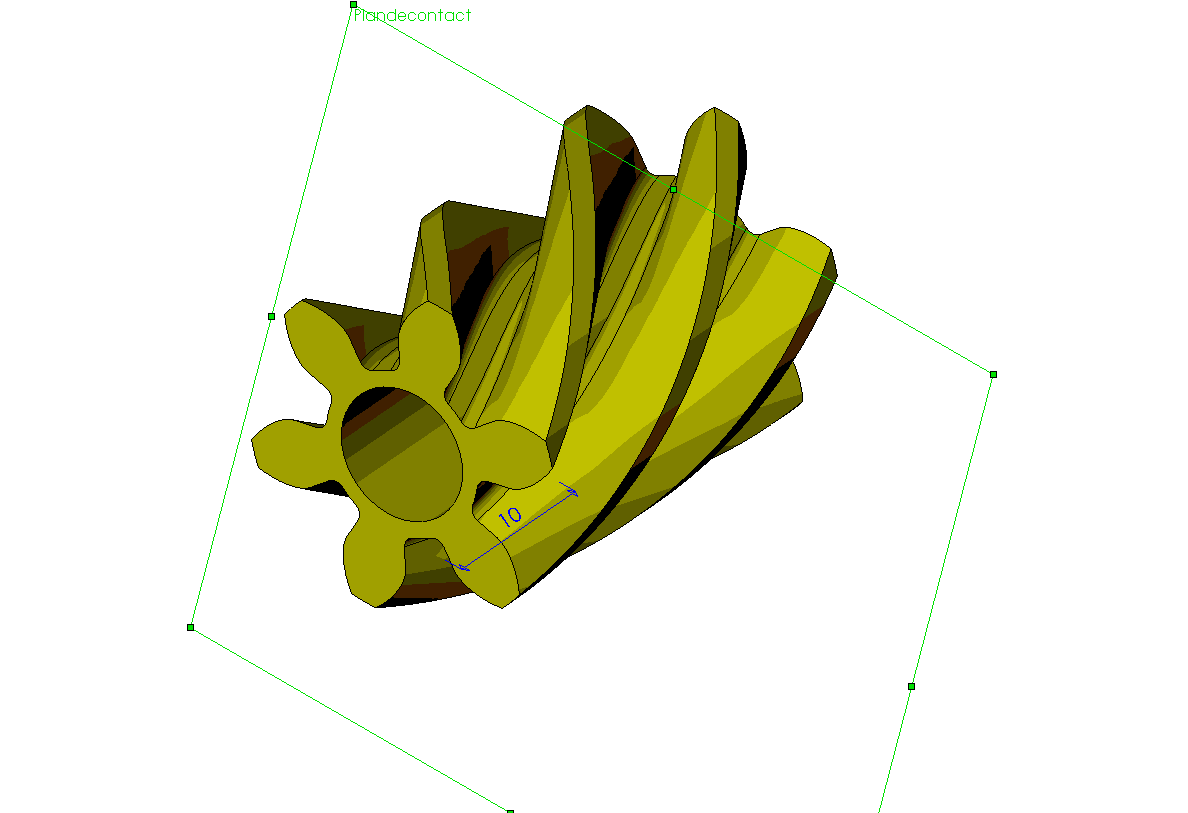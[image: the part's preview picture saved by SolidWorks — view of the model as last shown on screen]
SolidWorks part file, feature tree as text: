
SOLIDWORKS PART (.sldprt)
format: sldprt  version: not decoded by parser v0  size: 2,865,152 bytes
history: native  units: mm
features: sketch x9, plane x6, material x1, extrude x1, helix x1, sweep x1, pattern_circular x1, cut_extrude x1 (+8 scaffold rows collapsed)
feature tree (29):
  scaffold x8  (default folders/planes/origin — collapsed)
  material  "Matériau <non spécifié>"
  plane  "Plan1"
  plane  "Plan2"
  plane  "Plan3"
  plane  "Plandecontact"  Offset=10mm
  sketch  "def"  dims[c1.D1=10.0mm c1.D2=1.0mm c1.D3=1.0mm c1.D4=0.3mm c1.D5=~14.911604mm c2.D1=6.0mm c2.D6=~8.457328mm c2.D2=2.0mm c2.D7=~6.009154mm c2.D3=1.0mm c2.D8=~2.819109mm c2.D4=0.3mm c2.D5=25.0mm c3.D6=1.0mm c3.D7=30.0mm c3.D8=~13.540468mm c3.D9=~13.540468mm c4.D8=10.0mm]
  sketch  "var"  dims[D1=~22.795877mm D2=~2.309401mm]
  sketch  "diamtete"  dims[Dp=8.5mm D1=~17.856406mm]
  extrude  "Volume de tête"  Depth=25mm
  sketch  "dev"  dims[c1.D7=~10.198039mm c1.D8=~10.198039mm c2.D7=18.8mm c2.D9=20.0mm c3.D7=18.8mm c3.D10=~12.774097mm c3.D8=17.5mm c4.D10=17.5mm c4.D1=7.0mm c4.D2=6.0mm c4.D3=1.5mm c4.D4=11.0mm c5.D4=15.0deg c5.D5=11.0mm c6.D5=20.0deg c6.D6=11.0mm c7.D6=25.0deg c7.D1=2.2295mm c7.D2=~3.344251mm c7.D3=~4.459001mm c7.D4=11.0mm c7.A1=20.0deg c7.D5=11.0mm c7.A2=30.0deg c8.D6=11.0mm c8.A3=40.0deg c8.D8=~15.524175mm c9.D8=4.0deg c10.D8=10.0mm c11.D8=4.0deg c11.D10=10.0mm c12.D10=4.5deg c12.D8=1.0mm c12.D9=1.0mm c13.D8=9.4mm c13.A5=150.0deg c13.D9=~12.133892mm c13.D5=~16.721254mm c13.D10=~10.689046mm c13.D4=~5.573751mm c13.D11=9.4mm c13.A4=50.0deg c13.D12=18.8mm c13.D13=9.8418mm c13.D14=~2.897254mm c13.D32=~2.897254mm c13.D6=~6.888727mm c13.D7=~7.341507mm c14.D8=~7.438531mm c14.D34=~7.438531mm c15.D8=~7.57466mm c15.D6=14.1mm c15.A6=80.0deg c16.D6=~8.918002mm c16.D7=14.1mm c16.A7=120.0deg c17.D7=~13.377003mm c17.D8=~0.832758mm c17.D9=~1.80174mm c17.D11=~3.027617mm c17.D12=~4.387718mm c17.D13=~0.197414mm c17.D14=~0.656143mm c17.D15=~1.522129mm c17.D16=~2.891055mm c17.D17=1.0mm c18.D13=~1.089454mm c18.D14=~1.297318mm c18.D15=~1.689723mm c18.D16=~3.891055mm c18.D18=~0.832758mm c18.D19=~1.80174mm c18.D20=~3.004888mm c18.D21=~4.387718mm c18.D22=1.0mm c18.D23=1.0mm c18.D24=1.0mm c18.D25=~1.578211mm c18.D8=~4.73588mm c19.D8=100.0deg c20.D8=~13.350645mm c20.A0=~89.146042deg c20.D9=~13.350645mm c21.D8=~13.350645mm c21.A0=103.7158deg]
  sketch  "pied"  dims[c1.D1=20.0mm c1.D2=58.0mm c1.D4=0.6mm c1.D5=~15.704768mm c2.D4=0.6mm c2.D3=30.0mm c3.D4=0.6mm c3.D2=0.6mm c3.D1=0.6mm c4.D2=~8.856406mm c4.D3=~10.342124mm c5.D3=3.0deg c5.D5=~31.409536mm c6.D3=30.0mm c7.D3=3.0deg c8.D3=30.0mm c9.D3=9.0deg]
  sketch  "primitif"  dims[c1.D1=12.0mm c1.D2=7.4mm c2.D2=12.0deg]
  sketch  "profil"  dims[c1.D1=30.0mm c1.D2=58.0mm c1.D4=0.6mm c1.D5=~15.704768mm c2.D4=0.6mm c2.D3=30.0mm c3.D4=0.6mm c3.D2=0.6mm c3.D6=~75.066051mm c4.D2=27.0mm c4.D3=~10.342124mm c5.D3=3.0deg c5.D5=~31.409536mm c6.D3=30.0mm c7.D3=3.0deg c8.D3=30.0mm c9.D3=6.0deg c9.D2=4.25mm c9.D4=4.25mm c10.D4=12.0deg c10.D2=3.0mm c10.D1=~20.921979mm c11.D1=30.0deg c11.D3=3.0mm c11.D5=5.0mm]
  sketch  "Esquisse2"
  helix  "helice"  Pitch=25mm
  sweep  "Creux de dent"
  pattern_circular  "Répétition circulaire1"  Count=6 Angle=360deg
  sketch  "alésage"  dims[D1=~7.085125mm D2=44.0mm]
  cut_extrude  "centrage"  [1 undecoded]
  plane  "Plandecreux"
  plane  "Plan de dent"
decode coverage: 11 of 14 modeling features carry decoded parameters
note: ~ marks probable driven/reference dimensions
note: 1 parameter value undecoded
note: suppression state not decoded; provenance and decode notes live in map.json
